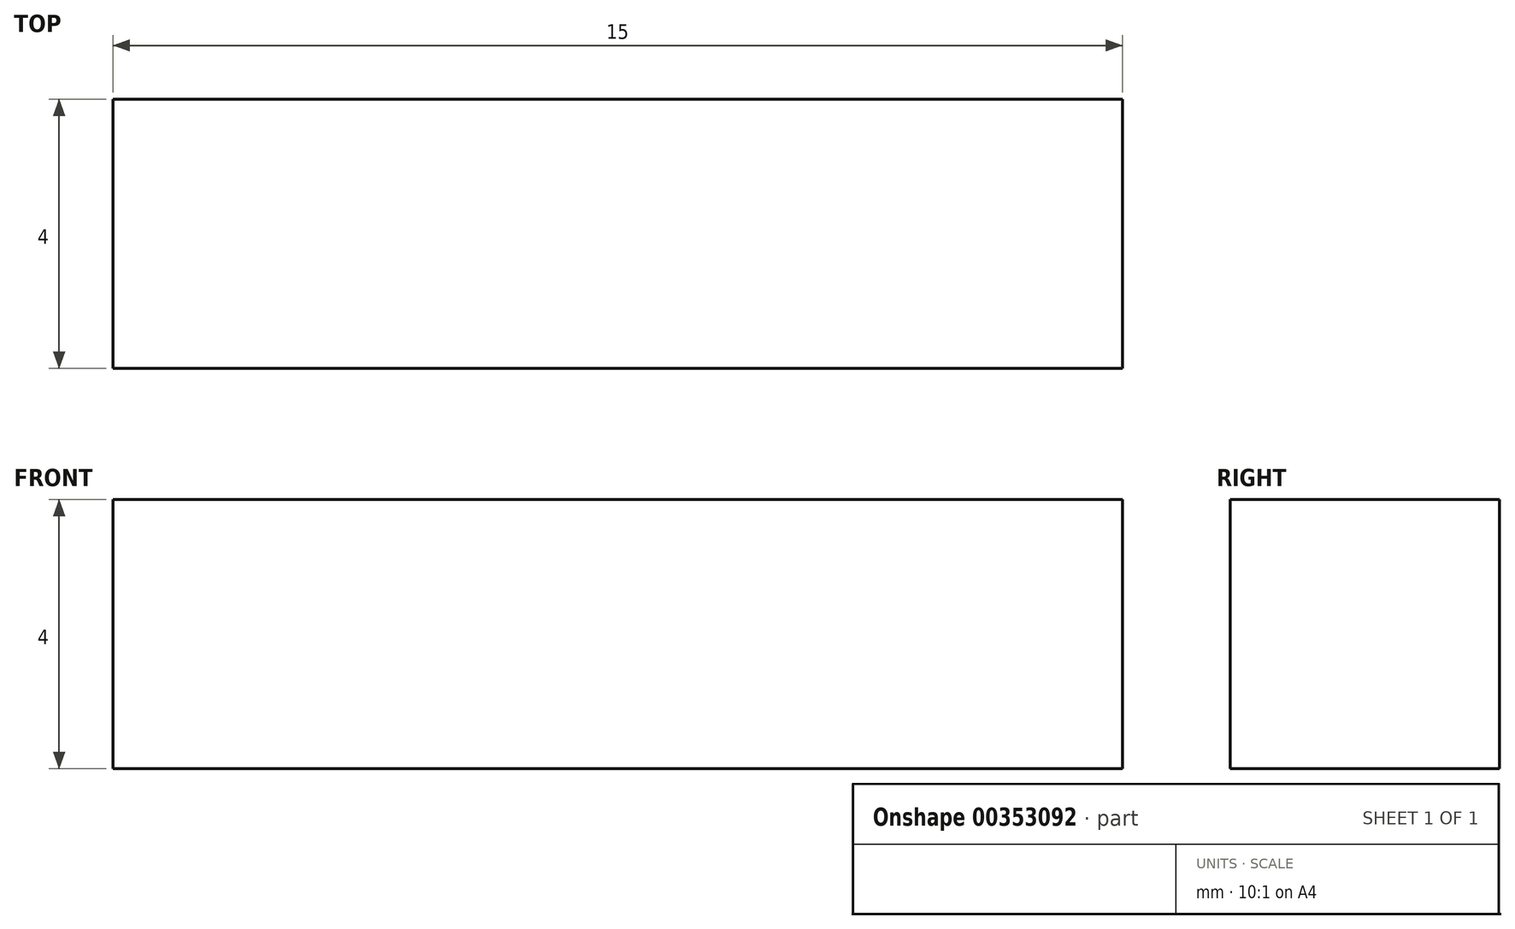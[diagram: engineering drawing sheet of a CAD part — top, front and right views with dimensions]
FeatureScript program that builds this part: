
annotation { "Feature Type Name" : "Feature", "Feature Type Description" : "" }
export const myFeature = defineFeature(function(context is Context, id is Id, definition is map)
    precondition{}
    {
        {
            var Q0;
            Q0=qCreatedBy(makeId("Top.planeOp"),FACE);
            var sketch = newSketch(context, id + "F0", { "sketchPlane" : qUnion([Q0])});
            skLineSegment(sketch, "E0.bottom", {"start": v(0, 0) * mm, "end": v(15, 0) * mm});
            skLineSegment(sketch, "E0.top", {"start": v(0, 4) * mm, "end": v(15, 4) * mm});
            skLineSegment(sketch, "E0.left", {"start": v(0, 0) * mm, "end": v(0, 4) * mm});
            skLineSegment(sketch, "E0.right", {"start": v(15, 0) * mm, "end": v(15, 4) * mm});
            skSolve(sketch);
        }
        {
            var Q0;
            Q0=makeQuery(id+"F0.imprint","IMPRINT",FACE,{"disambiguationData":[TD([[makeQuery(id+"F0.imprint","IMPRINT",EDGE,{"derivedFrom":sQuery(id+"F0.wireOp",EDGE,"E0.bottom")}),1.0]])]});
            extrude(context, id + "F1", {"entities" : qUnion([Q0]), "depth" : 4 * mm});
        }
    });
